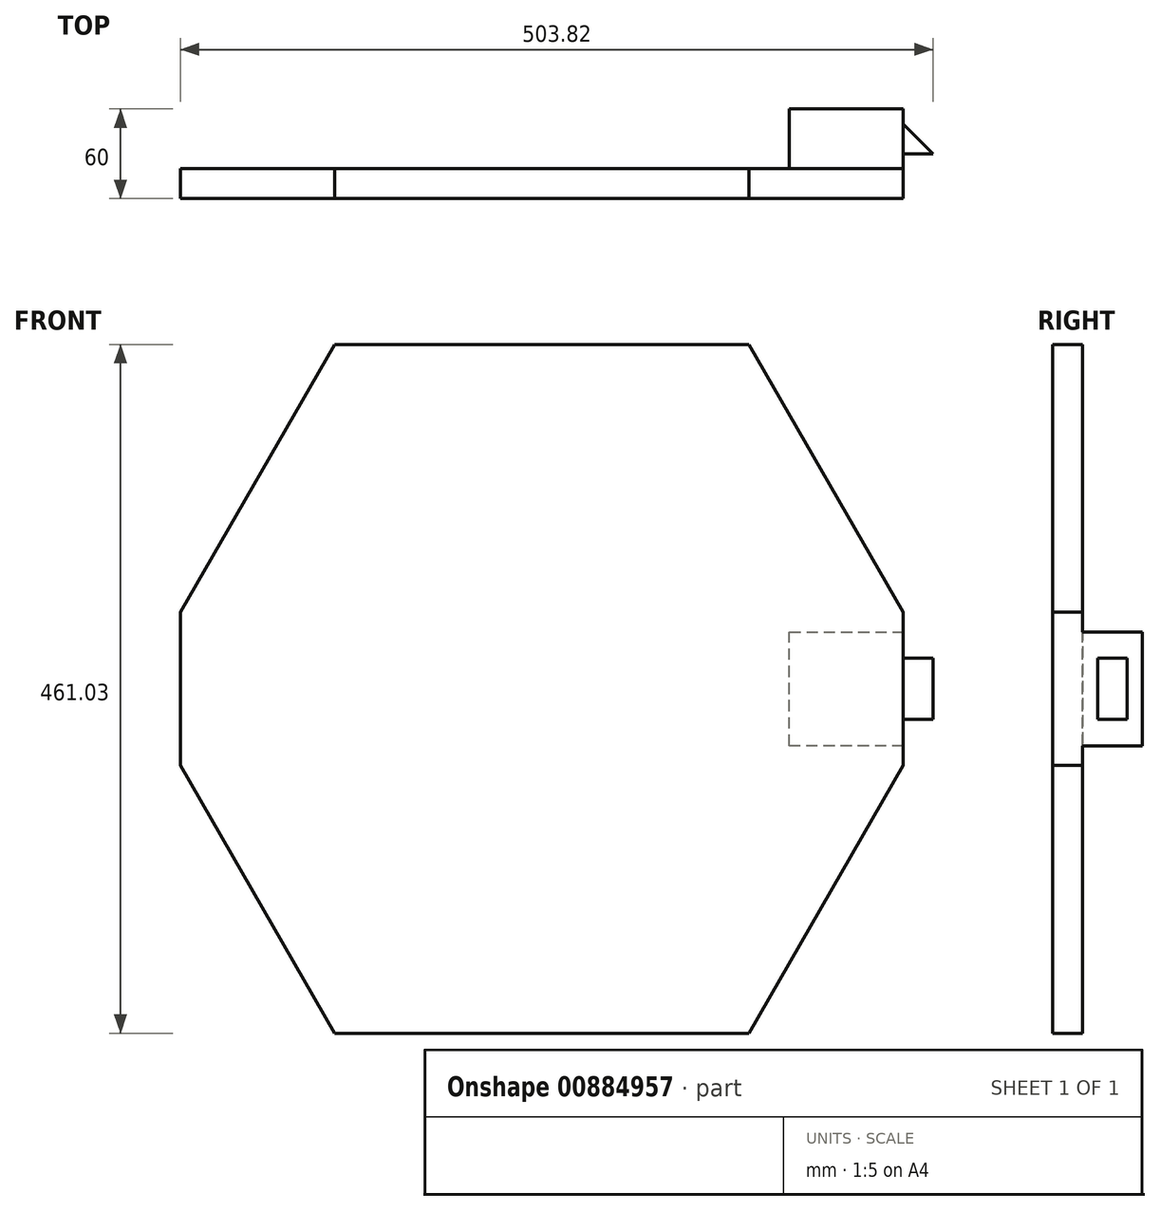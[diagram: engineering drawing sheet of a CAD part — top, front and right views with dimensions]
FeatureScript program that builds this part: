
annotation { "Feature Type Name" : "Feature", "Feature Type Description" : "" }
export const myFeature = defineFeature(function(context is Context, id is Id, definition is map)
    precondition{}
    {
        {
            var Q0;
            Q0=qCreatedBy(makeId("Front.planeOp"),FACE);
            var sketch = newSketch(context, id + "F0", { "sketchPlane" : qUnion([Q0])});
            skLineSegment(sketch, "E0", {"start": v(-154.98, 229.68) * mm, "end": v(121.93, 229.68) * mm});
            skLineSegment(sketch, "E1", {"start": v(121.93, -231.35) * mm, "end": v(-154.98, -231.35) * mm});
            skLineSegment(sketch, "E2", {"start": v(-154.98, 229.68) * mm, "end": v(-258.44, 50.5) * mm});
            skLineSegment(sketch, "E3", {"start": v(-258.44, 50.5) * mm, "end": v(-258.44, -52.17) * mm});
            skLineSegment(sketch, "E4", {"start": v(-258.44, -52.17) * mm, "end": v(-154.98, -231.35) * mm});
            skLineSegment(sketch, "E5", {"start": v(121.93, 229.68) * mm, "end": v(225.38, 50.5) * mm});
            skLineSegment(sketch, "E6", {"start": v(225.38, 50.5) * mm, "end": v(225.38, -52.17) * mm});
            skLineSegment(sketch, "E7", {"start": v(225.38, -52.17) * mm, "end": v(121.93, -231.35) * mm});
            skSolve(sketch);
        }
        {
            var Q0;
            Q0=makeQuery(id+"F0.imprint","IMPRINT",FACE,{"disambiguationData":[TD([[makeQuery(id+"F0.imprint","IMPRINT",EDGE,{"derivedFrom":sQuery(id+"F0.wireOp",EDGE,"E0")}),-1.0]])]});
            extrude(context, id + "F1", {"entities" : qUnion([Q0]), "depth" : 20 * mm, "offsetDistance" : 25.4 * mm});
        }
        {
            var Q0;
            Q0=makeQuery(id+"F1.opExtrude","CAP_FACE",FACE,{"disambiguationData":[OSD([sQuery(id+"F0.wireOp",EDGE,"E0"),sQuery(id+"F0.wireOp",EDGE,"c9oIbuxj-U33o-cYR5-rHRN-VFZxlMwbOOmB"),sQuery(id+"F0.wireOp",EDGE,"5bhXoy1V-4mnx-wVRy-pG6D-friqmlpx8n7M"),sQuery(id+"F0.wireOp",EDGE,"E1"),sQuery(id+"F0.wireOp",EDGE,"o2sicSU0-sXp8-bxxk-FAbK-nBmEM2bLMAtQ"),sQuery(id+"F0.wireOp",EDGE,"4YcediaQ-mSxV-85Rg-PTlz-l7TXPk9ntIwF")])],"isStart":true});
            var sketch = newSketch(context, id + "F2", { "sketchPlane" : qUnion([Q0])});
            skLineSegment(sketch, "E8", {"start": v(-225.38, 37.28) * mm, "end": v(-225.38, -38.92) * mm});
            skLineSegment(sketch, "E9", {"start": v(-225.38, -38.92) * mm, "end": v(-149.18, -38.92) * mm});
            skLineSegment(sketch, "E10", {"start": v(-149.18, -38.92) * mm, "end": v(-149.18, 37.28) * mm});
            skLineSegment(sketch, "E11", {"start": v(-149.18, 37.28) * mm, "end": v(-225.38, 37.28) * mm});
            skSolve(sketch);
        }
        {
            var Q0;
            Q0 = qSketchRegion(id + "F2", true);
            extrude(context, id + "F3", {"entities" : qUnion([Q0]), "operationType" : NewBodyOperationType.ADD, "depth" : 40 * mm, "offsetDistance" : 25.4 * mm});
        }
        {
            var Q0;
            Q0=makeQuery(id+"F3.opExtrude","SWEPT_FACE",FACE,{"disambiguationData":[OSD([sQuery(id+"F2.wireOp",EDGE,"E8")])]});
            var sketch = newSketch(context, id + "F4", { "sketchPlane" : qUnion([Q0])});
            skLineSegment(sketch, "E12", {"start": v(9.9, 19.8) * mm, "end": v(29.9, 19.8) * mm});
            skLineSegment(sketch, "E13", {"start": v(29.9, 19.8) * mm, "end": v(29.9, -21.44) * mm});
            skLineSegment(sketch, "E14", {"start": v(29.9, -21.44) * mm, "end": v(9.9, -21.44) * mm});
            skLineSegment(sketch, "E15", {"start": v(9.9, -21.44) * mm, "end": v(9.9, 19.8) * mm});
            skSolve(sketch);
        }
        {
            var Q0;
            Q0 = qSketchRegion(id + "F4", true);
            extrude(context, id + "F5", {"entities" : qUnion([Q0]), "operationType" : NewBodyOperationType.ADD, "depth" : 20 * mm, "offsetDistance" : 25.4 * mm});
        }
        {
            var Q0;
            Q0=makeQuery(id+"F5.opExtrude","SWEPT_FACE",FACE,{"disambiguationData":[OSD([sQuery(id+"F4.wireOp",EDGE,"E12")])]});
            var sketch = newSketch(context, id + "F6", { "sketchPlane" : qUnion([Q0])});
            skLineSegment(sketch, "E16", {"start": v(225.38, 29.9) * mm, "end": v(245.38, 9.9) * mm});
            skLineSegment(sketch, "E17", {"start": v(245.38, 9.9) * mm, "end": v(245.38, 29.9) * mm});
            skLineSegment(sketch, "E18", {"start": v(245.38, 29.9) * mm, "end": v(225.38, 29.9) * mm});
            skSolve(sketch);
        }
        {
            var Q0;
            Q0 = qSketchRegion(id + "F6", true);
            extrude(context, id + "F7", {"entities" : qUnion([Q0]), "operationType" : NewBodyOperationType.REMOVE, "endBound" : BoundingType.THROUGH_ALL, "oppositeDirection" : true, "depth" : 25.4 * mm, "offsetDistance" : 25.4 * mm});
        }
    });
